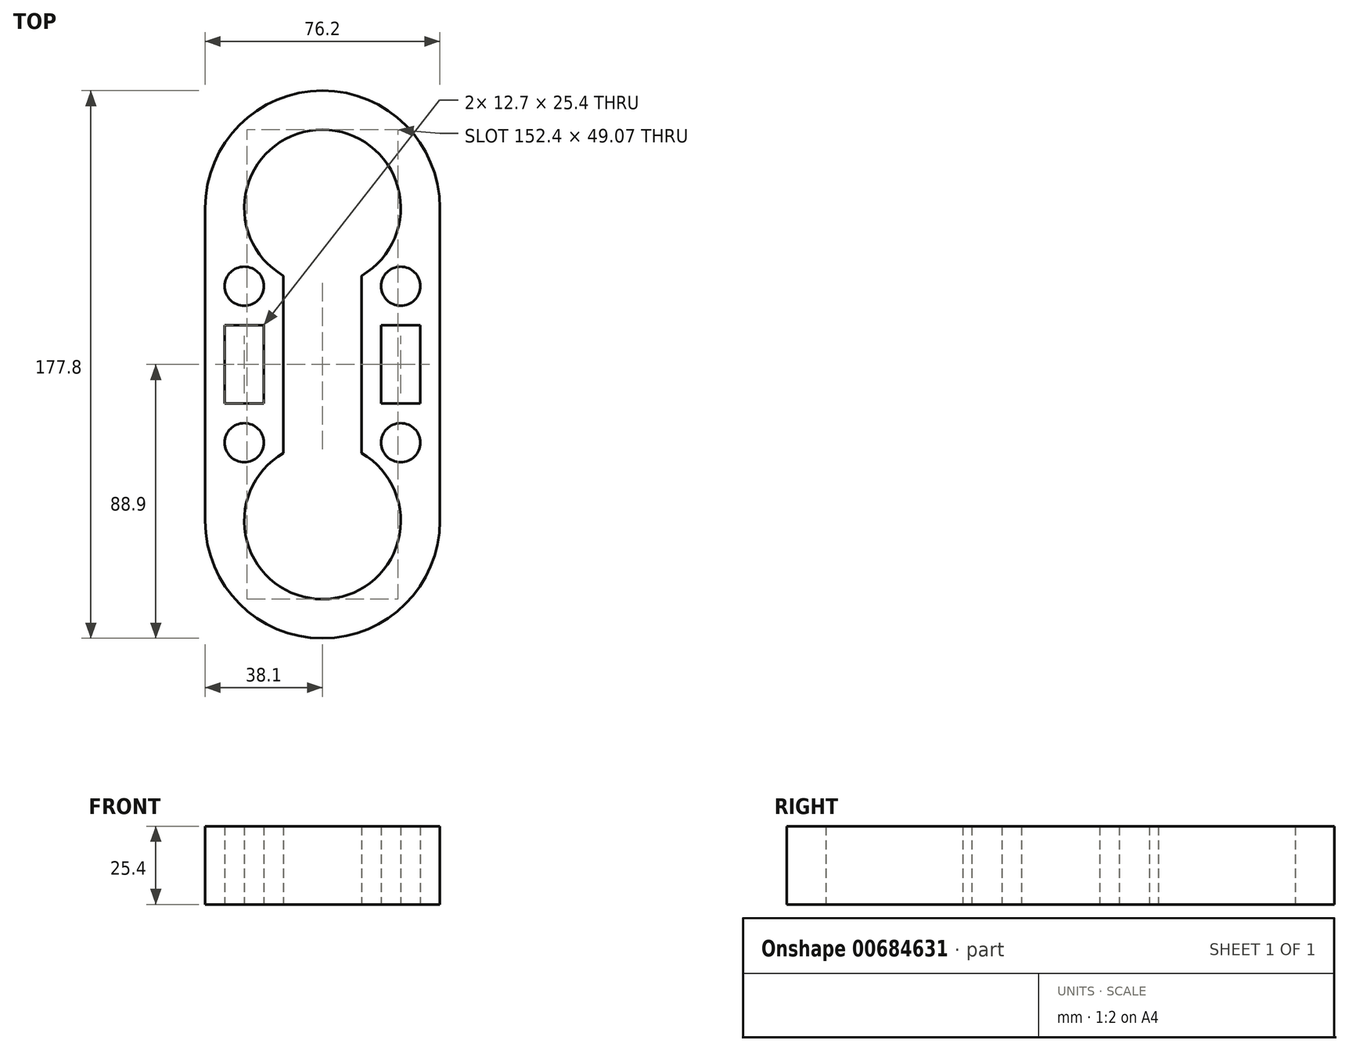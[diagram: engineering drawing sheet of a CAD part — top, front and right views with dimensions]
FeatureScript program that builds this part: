
annotation { "Feature Type Name" : "Feature", "Feature Type Description" : "" }
export const myFeature = defineFeature(function(context is Context, id is Id, definition is map)
    precondition{}
    {
        {
            var Q0;
            Q0=qCreatedBy(makeId("Top.planeOp"),FACE);
            var sketch = newSketch(context, id + "F0", { "sketchPlane" : qUnion([Q0])});
            skLineSegment(sketch, "E0", {"start": v(-38.1, 50.8) * mm, "end": v(-38.1, -50.8) * mm});
            skLineSegment(sketch, "E1", {"start": v(38.1, 50.8) * mm, "end": v(38.1, -50.8) * mm});
            skArc(sketch, "E2", {"start": v(38.1, 50.8) * mm, "mid": v(0, 88.9) * mm, "end": v(-38.1, 50.8) * mm});
            skArc(sketch, "E3", {"start": v(-38.1, -50.8) * mm, "mid": v(0, -88.9) * mm, "end": v(38.1, -50.8) * mm});
            skLineSegment(sketch, "E4", {"start": v(-12.7, 28.8) * mm, "end": v(-12.7, -28.8) * mm});
            skLineSegment(sketch, "E5", {"start": v(12.7, 28.8) * mm, "end": v(12.7, -28.8) * mm});
            skArc(sketch, "E6", {"start": v(12.7, 28.8) * mm, "mid": v(0, 76.2) * mm, "end": v(-12.7, 28.8) * mm});
            skArc(sketch, "E7", {"start": v(-12.7, -28.8) * mm, "mid": v(0, -76.2) * mm, "end": v(12.7, -28.8) * mm});
            skCircle(sketch, "E8", {"center": v(-25.4, 25.4) * mm, "radius": 6.35 * mm});
            skCircle(sketch, "E9", {"center": v(25.4, 25.4) * mm, "radius": 6.35 * mm});
            skCircle(sketch, "E10", {"center": v(25.4, -25.4) * mm, "radius": 6.35 * mm});
            skCircle(sketch, "E11", {"center": v(-25.4, -25.4) * mm, "radius": 6.35 * mm});
            skLineSegment(sketch, "E12", {"start": v(-31.75, 12.7) * mm, "end": v(-19.05, 12.7) * mm});
            skLineSegment(sketch, "E13", {"start": v(-19.05, 12.7) * mm, "end": v(-19.05, -12.7) * mm});
            skLineSegment(sketch, "E14", {"start": v(-19.05, -12.7) * mm, "end": v(-31.75, -12.7) * mm});
            skLineSegment(sketch, "E15", {"start": v(-31.75, -12.7) * mm, "end": v(-31.75, 12.7) * mm});
            skLineSegment(sketch, "E16", {"start": v(19.05, 12.7) * mm, "end": v(31.75, 12.7) * mm});
            skLineSegment(sketch, "E17", {"start": v(31.75, 12.7) * mm, "end": v(31.75, -12.7) * mm});
            skLineSegment(sketch, "E18", {"start": v(31.75, -12.7) * mm, "end": v(19.05, -12.7) * mm});
            skLineSegment(sketch, "E19", {"start": v(19.05, -12.7) * mm, "end": v(19.05, 12.7) * mm});
            skSolve(sketch);
        }
        {
            var Q0;
            Q0 = qSketchRegion(id + "F0", true);
            extrude(context, id + "F1", {"entities" : qUnion([Q0]), "depth" : 25.4 * mm, "offsetDistance" : 25.4 * mm});
        }
    });
